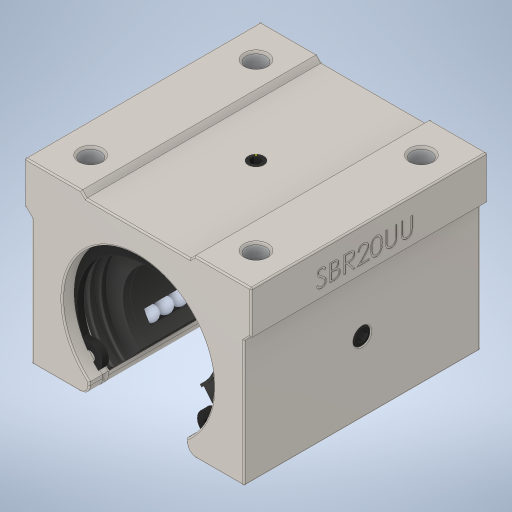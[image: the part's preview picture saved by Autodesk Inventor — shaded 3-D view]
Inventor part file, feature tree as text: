
AUTODESK INVENTOR PART (.ipt)
format: ipt  version: 2023.5 (Build 275446000, 446)  size: 2,190,848 bytes
history: imported  units: in
note: dims shown in document units (in); Inventor stores cm internally (conversion verified against a paired STEP export)
features: other x51, sketch x1, imported_body x1
ambient origin geometry x8: Origin, YZ Plane, XZ Plane, XY Plane, X Axis, Y Axis, Z Axis, Center Point
bodies: Solid1 (imported_parasolid), Solid2 (imported_parasolid), Solid3 (imported_parasolid), Solid4 (imported_parasolid), Solid5 (imported_parasolid), Solid6 (imported_parasolid), Solid7 (imported_parasolid), Solid8 (imported_parasolid), Solid9 (imported_parasolid), Solid10 (imported_parasolid), Solid11 (imported_parasolid), Solid12 (imported_parasolid), Solid13 (imported_parasolid), Solid14 (imported_parasolid), Solid15 (imported_parasolid), Solid16 (imported_parasolid), Solid17 (imported_parasolid), Solid18 (imported_parasolid), Solid19 (imported_parasolid), Solid20 (imported_parasolid), Solid21 (imported_parasolid), Solid22 (imported_parasolid), Solid23 (imported_parasolid), Solid24 (imported_parasolid), Solid25 (imported_parasolid), Solid26 (imported_parasolid), Solid27 (imported_parasolid), Solid28 (imported_parasolid), Solid29 (imported_parasolid), Solid30 (imported_parasolid), Solid31 (imported_parasolid), Solid32 (imported_parasolid), Solid33 (imported_parasolid), Solid34 (imported_parasolid), Solid35 (imported_parasolid), Solid36 (imported_parasolid), Solid37 (imported_parasolid), Solid38 (imported_parasolid), Solid39 (imported_parasolid), Solid40 (imported_parasolid), Solid41 (imported_parasolid), Solid42 (imported_parasolid), Solid43 (imported_parasolid), Solid44 (imported_parasolid), Solid45 (imported_parasolid), Solid46 (imported_parasolid), Solid47 (imported_parasolid), Solid48 (imported_parasolid), Solid49 (imported_parasolid), Solid50 (imported_parasolid), Solid51 (imported_parasolid)
feature tree (53):
  sketch  "草图1"  dims[d0=0.0197in d1=0.0344in d2=0.0197in d3=0.0344in]
  other  "M4 Tapped Hole2"
  other  "_Retaining clip sbr20_-_Boss-Extrude1_"
  other  "_Retaining clip sbr20_-_Boss-Extrude1_:1"
  other  "_SBR20 - bearing insert_-_CirPattern6_"
  other  "_SBR20 - bearing insert_-_Revolve4_"
  other  "_SBR20 - bearing insert_-_LPattern4[1]_"
  other  "_SBR20 - bearing insert_-_LPattern4[2]_"
  other  "_SBR20 - bearing insert_-_LPattern4[3]_"
  other  "_SBR20 - bearing insert_-_LPattern4[4]_"
  other  "_SBR20 - bearing insert_-_LPattern4[5]_"
  other  "_SBR20 - bearing insert_-_LPattern4[6]_"
  other  "_SBR20 - bearing insert_-_LPattern4[7]_"
  other  "_SBR20 - bearing insert_-_LPattern4[8]_"
  other  "_SBR20 - bearing insert_-_CirPattern8[1]_"
  other  "_SBR20 - bearing insert_-_CirPattern8[2]_"
  other  "_SBR20 - bearing insert_-_CirPattern8[3]_"
  other  "_SBR20 - bearing insert_-_CirPattern8[4]_"
  other  "_SBR20 - bearing insert_-_CirPattern8[5]_"
  other  "_SBR20 - bearing insert_-_CirPattern8[6]_"
  other  "_SBR20 - bearing insert_-_CirPattern8[7]_"
  other  "_SBR20 - bearing insert_-_CirPattern8[8]_"
  other  "_SBR20 - bearing insert_-_CirPattern8[9]_"
  other  "_SBR20 - bearing insert_-_CirPattern8[10]_"
  other  "_SBR20 - bearing insert_-_CirPattern8[11]_"
  other  "_SBR20 - bearing insert_-_CirPattern8[12]_"
  other  "_SBR20 - bearing insert_-_CirPattern8[13]_"
  other  "_SBR20 - bearing insert_-_CirPattern8[14]_"
  other  "_SBR20 - bearing insert_-_CirPattern8[15]_"
  other  "_SBR20 - bearing insert_-_CirPattern8[16]_"
  other  "_SBR20 - bearing insert_-_CirPattern8[17]_"
  other  "_SBR20 - bearing insert_-_CirPattern8[18]_"
  other  "_SBR20 - bearing insert_-_CirPattern8[19]_"
  other  "_SBR20 - bearing insert_-_CirPattern8[20]_"
  other  "_SBR20 - bearing insert_-_CirPattern8[21]_"
  other  "_SBR20 - bearing insert_-_CirPattern8[22]_"
  other  "_SBR20 - bearing insert_-_CirPattern8[23]_"
  other  "_SBR20 - bearing insert_-_CirPattern8[24]_"
  other  "_SBR20 - bearing insert_-_CirPattern8[25]_"
  other  "_SBR20 - bearing insert_-_CirPattern8[26]_"
  other  "_SBR20 - bearing insert_-_CirPattern8[27]_"
  other  "_SBR20 - bearing insert_-_CirPattern8[28]_"
  other  "_SBR20 - bearing insert_-_CirPattern8[29]_"
  other  "_SBR20 - bearing insert_-_CirPattern8[30]_"
  other  "_SBR20 - bearing insert_-_CirPattern8[31]_"
  other  "_SBR20 - bearing insert_-_CirPattern8[32]_"
  other  "_SBR20 - bearing insert_-_CirPattern8[33]_"
  other  "_SBR20 - bearing insert_-_CirPattern8[34]_"
  other  "_SBR20 - bearing insert_-_CirPattern8[35]_"
  other  "_SBR20 - bearing insert_-_CirPattern8[36]_"
  other  "_DIN 916 - M4 x 5-N_-_Hex_"
  other  "_DIN 916 - M4 x 5-N_-_Hex_:1"
  imported_body  NMx_Import_Brep_tag  [imported B-rep: ~65 faces, bbox_mm=None]
